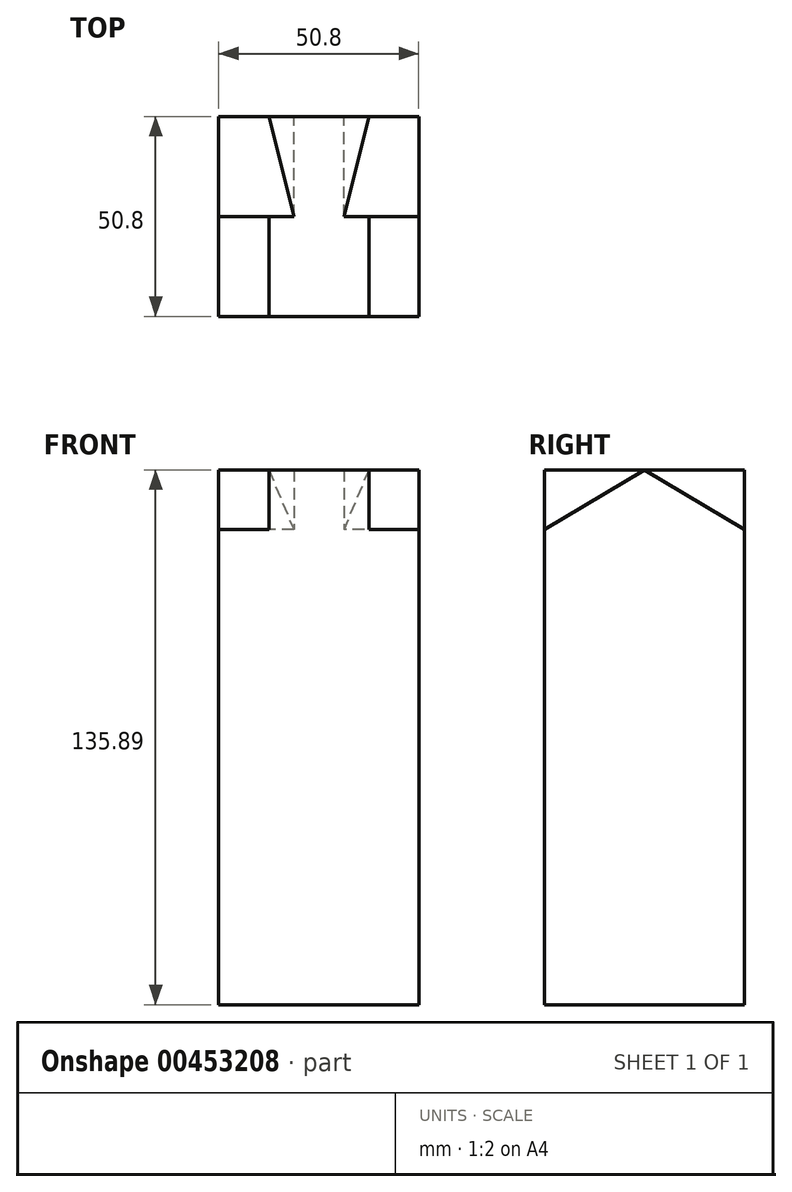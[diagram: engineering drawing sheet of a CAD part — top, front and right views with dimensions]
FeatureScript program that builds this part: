
annotation { "Feature Type Name" : "Feature", "Feature Type Description" : "" }
export const myFeature = defineFeature(function(context is Context, id is Id, definition is map)
    precondition{}
    {
        {
            var Q0;
            Q0=qCreatedBy(makeId("Top.planeOp"),FACE);
            var sketch = newSketch(context, id + "F0", { "sketchPlane" : qUnion([Q0])});
            skLineSegment(sketch, "E0.bottom", {"start": v(30.23, -20.65) * mm, "end": v(-20.57, -20.65) * mm});
            skLineSegment(sketch, "E0.top", {"start": v(30.23, 30.15) * mm, "end": v(-20.57, 30.15) * mm});
            skLineSegment(sketch, "E0.left", {"start": v(30.23, -20.65) * mm, "end": v(30.23, 30.15) * mm});
            skLineSegment(sketch, "E0.right", {"start": v(-20.57, -20.65) * mm, "end": v(-20.57, 30.15) * mm});
            skSolve(sketch);
        }
        {
            var Q0;
            Q0=makeQuery(id+"F0.imprint","IMPRINT",FACE,{"disambiguationData":[TD([[makeQuery(id+"F0.imprint","IMPRINT",EDGE,{"derivedFrom":sQuery(id+"F0.wireOp",EDGE,"E0.bottom")}),-1.0]])]});
            extrude(context, id + "F1", {"entities" : qUnion([Q0]), "depth" : 135.89 * mm});
        }
        {
            var Q0;
            Q0=makeQuery(id+"F1.opExtrude","SWEPT_FACE",FACE,{"disambiguationData":[OSD([sQuery(id+"F0.wireOp",EDGE,"E0.top")])]});
            var sketch = newSketch(context, id + "F2", { "sketchPlane" : qUnion([Q0])});
            skLineSegment(sketch, "E1", {"start": v(-17.53, 135.9) * mm, "end": v(-11.18, 120.72) * mm});
            skLineSegment(sketch, "E2", {"start": v(7.87, 135.9) * mm, "end": v(1.52, 120.72) * mm});
            skLineSegment(sketch, "E3", {"start": v(-11.18, 120.72) * mm, "end": v(1.52, 120.72) * mm});
            skLineSegment(sketch, "E4", {"start": v(-11.18, 120.72) * mm, "end": v(-30.23, 120.72) * mm});
            skLineSegment(sketch, "E5", {"start": v(1.52, 120.72) * mm, "end": v(20.57, 120.72) * mm});
            skSolve(sketch);
        }
        {
            var Q0;
            Q0=makeQuery(id+"F1.opExtrude","SWEPT_FACE",FACE,{"disambiguationData":[OSD([sQuery(id+"F0.wireOp",EDGE,"E0.right")])]});
            var sketch = newSketch(context, id + "F3", { "sketchPlane" : qUnion([Q0])});
            skLineSegment(sketch, "E6", {"start": v(-30.15, 120.72) * mm, "end": v(-4.75, 135.9) * mm});
            skLineSegment(sketch, "E7", {"start": v(-4.75, 135.9) * mm, "end": v(20.65, 120.72) * mm});
            skSolve(sketch);
        }
        {
            var Q0;
            Q0=makeQuery(id+"F1.opExtrude","CAP_FACE",FACE,{"disambiguationData":[OSD([sQuery(id+"F0.wireOp",EDGE,"E0.bottom"),sQuery(id+"F0.wireOp",EDGE,"E0.top"),sQuery(id+"F0.wireOp",EDGE,"E0.left"),sQuery(id+"F0.wireOp",EDGE,"E0.right")])],"isStart":false});
            var sketch = newSketch(context, id + "F4", { "sketchPlane" : qUnion([Q0])});
            skLineSegment(sketch, "E8", {"start": v(-7.87, 30.15) * mm, "end": v(-7.87, -20.65) * mm});
            skLineSegment(sketch, "E9", {"start": v(17.53, 30.15) * mm, "end": v(17.53, -20.65) * mm});
            skLineSegment(sketch, "E10", {"start": v(-20.57, 4.75) * mm, "end": v(30.23, 4.75) * mm});
            skLineSegment(sketch, "E11", {"start": v(17.53, 30.15) * mm, "end": v(11.18, 4.75) * mm});
            skLineSegment(sketch, "E12", {"start": v(11.18, 4.75) * mm, "end": v(-1.52, 4.75) * mm});
            skLineSegment(sketch, "E13", {"start": v(-1.52, 4.75) * mm, "end": v(-7.87, 30.15) * mm});
            skLineSegment(sketch, "E14", {"start": v(11.18, 4.75) * mm, "end": v(30.23, 4.75) * mm});
            skLineSegment(sketch, "E15", {"start": v(-1.52, 4.75) * mm, "end": v(-20.57, 4.75) * mm});
            skSolve(sketch);
        }
        {
            var Q0;
            {var subQ4=sQuery(id+"F3.wireOp",EDGE,"E6");Q0=makeQuery(id+"F3.imprint","IMPRINT",FACE,{"disambiguationData":[TD([[makeQuery(id+"F3.imprint","IMPRINT",EDGE,{"derivedFrom":subQ4}),-1.0]])]});}
            var sketch = newSketch(context, id + "F5", { "sketchPlane" : qUnion([Q0])});
            skLineSegment(sketch, "E16", {"start": v(-4.75, 135.9) * mm, "end": v(-4.75, 120.72) * mm});
            skLineSegment(sketch, "E17", {"start": v(-4.75, 120.72) * mm, "end": v(-30.15, 120.72) * mm});
            skLineSegment(sketch, "E18", {"start": v(-4.75, 135.9) * mm, "end": v(-30.15, 120.72) * mm});
            skSolve(sketch);
        }
        {
            var Q0;
            Q0 = qSketchRegion(id + "F5", true);
            var Q1;
            {var subQ0=sQuery(id+"F3.wireOp",EDGE,"E6");Q1=makeQuery(id+"F3.imprint","IMPRINT",FACE,{"disambiguationData":[TD([[makeQuery(id+"F3.imprint","IMPRINT",EDGE,{"derivedFrom":subQ0}),1.0]])]});}
            extrude(context, id + "F6", {"entities" : qUnion([Q0, Q1]), "operationType" : NewBodyOperationType.REMOVE, "oppositeDirection" : true, "depth" : 50.8 * mm});
        }
        {
            var Q0;
            Q0=makeQuery(id+"F6.boolean.opBoolean","COPY",FACE,{"derivedFrom":makeQuery(id+"F6.opExtrude","SWEPT_FACE",FACE,{"disambiguationData":[OSD([sQuery(id+"F5.wireOp",EDGE,"E16")])]})});
            var sketch = newSketch(context, id + "F7", { "sketchPlane" : qUnion([Q0])});
            skLineSegment(sketch, "E19", {"start": v(-11.18, 135.9) * mm, "end": v(-11.18, 120.72) * mm});
            skSolve(sketch);
        }
        {
            var Q0;
            Q0=makeQuery(id+"F6.boolean.opBoolean","COPY",FACE,{"derivedFrom":makeQuery(id+"F6.opExtrude","SWEPT_FACE",FACE,{"disambiguationData":[OSD([sQuery(id+"F5.wireOp",EDGE,"E17")])]})});
            var sketch = newSketch(context, id + "F8", { "sketchPlane" : qUnion([Q0])});
            skLineSegment(sketch, "E20", {"start": v(11.18, 30.15) * mm, "end": v(11.18, 4.75) * mm});
            skSolve(sketch);
        }
        {
            var Q0;
            {var subQ0=sQuery(id+"F7.wireOp",EDGE,"E19");Q0=makeQuery(id+"F7.imprint","IMPRINT",FACE,{"disambiguationData":[TD([[makeQuery(id+"F7.imprint","IMPRINT",EDGE,{"derivedFrom":subQ0}),1.0]])]});}
            var sketch = newSketch(context, id + "F9", { "sketchPlane" : qUnion([Q0])});
            skLineSegment(sketch, "E21", {"start": v(1.52, 135.9) * mm, "end": v(1.52, 120.72) * mm});
            skSolve(sketch);
        }
        {
            var Q0;
            {var subQ0=sQuery(id+"F8.wireOp",EDGE,"E20");Q0=makeQuery(id+"F8.imprint","IMPRINT",FACE,{"disambiguationData":[TD([[makeQuery(id+"F8.imprint","IMPRINT",EDGE,{"derivedFrom":subQ0}),-1.0]])]});}
            var sketch = newSketch(context, id + "F10", { "sketchPlane" : qUnion([Q0])});
            skLineSegment(sketch, "E22", {"start": v(-1.52, 4.75) * mm, "end": v(-1.52, 30.15) * mm});
            skSolve(sketch);
        }
        {
            var Q0;
            {var subQ0=sQuery(id+"F2.wireOp",EDGE,"E1");Q0=makeQuery(id+"F2.imprint","IMPRINT",FACE,{"disambiguationData":[TD([[makeQuery(id+"F2.imprint","IMPRINT",EDGE,{"derivedFrom":subQ0}),1.0]])]});}
            var sketch = newSketch(context, id + "F11", { "sketchPlane" : qUnion([Q0])});
            skLineSegment(sketch, "E23", {"start": v(-11.18, 135.9) * mm, "end": v(1.52, 135.9) * mm});
            skLineSegment(sketch, "E24", {"start": v(1.52, 135.9) * mm, "end": v(1.52, 120.72) * mm});
            skLineSegment(sketch, "E25", {"start": v(1.52, 120.72) * mm, "end": v(-11.18, 120.72) * mm});
            skLineSegment(sketch, "E26", {"start": v(-11.18, 120.72) * mm, "end": v(-11.18, 135.9) * mm});
            skSolve(sketch);
        }
        {
            var Q0;
            Q0=makeQuery(id+"F11.imprint","IMPRINT",FACE,{"disambiguationData":[TD([[makeQuery(id+"F11.imprint","IMPRINT",EDGE,{"derivedFrom":sQuery(id+"F11.wireOp",EDGE,"E23")}),-1.0]])]});
            extrude(context, id + "F12", {"entities" : qUnion([Q0]), "operationType" : NewBodyOperationType.ADD, "oppositeDirection" : true, "depth" : 27.71 * mm});
        }
        {
            var Q0;
            {var subQ0=sQuery(id+"F2.wireOp",EDGE,"E1");Q0=makeQuery(id+"F2.imprint","IMPRINT",FACE,{"disambiguationData":[TD([[makeQuery(id+"F2.imprint","IMPRINT",EDGE,{"derivedFrom":subQ0}),1.0]])]});}
            extrude(context, id + "F13", {"entities" : qUnion([Q0]), "operationType" : NewBodyOperationType.ADD, "oppositeDirection" : true, "depth" : 36.9 * mm});
        }
        {
            var Q0;
            {var subQ0=sQuery(id+"F4.wireOp",EDGE,"E11");Q0=makeQuery(id+"F4.imprint","IMPRINT",FACE,{"disambiguationData":[TD([[makeQuery(id+"F4.imprint","IMPRINT",EDGE,{"derivedFrom":subQ0}),1.0]])]});}
            extrude(context, id + "F14", {"entities" : qUnion([Q0]), "operationType" : NewBodyOperationType.REMOVE, "endBound" : BoundingType.UP_TO_NEXT, "oppositeDirection" : true, "depth" : 14.83 * mm});
        }
        {
            var Q0;
            Q0=sQuery(id+"F7.wireOp",VERTEX,"E19.start");
            var Q1;
            Q1=sQuery(id+"F8.wireOp",VERTEX,"E20.start");
            var Q2;
            {var subQ0=sQuery(id+"F2.wireOp",EDGE,"E1");Q2=makeQuery(id+"F14.boolean.opBoolean","MERGE",VERTEX,{"derivedFrom":[makeQuery(id+"F13.opExtrude","CAP_VERTEX",VERTEX,{"disambiguationData":[OSD([sQuery(id+"F0.wireOp",EDGE,"E0.top"),subQ0])],"isStart":true}),makeQuery(id+"F14.opExtrude","CAP_VERTEX",VERTEX,{"disambiguationData":[OSD([subQ0,sQuery(id+"F4.wireOp",EDGE,"E9"),sQuery(id+"F4.wireOp",EDGE,"E11"),sQuery(id+"F4.wireOp",EDGE,"E14")])],"isStart":false})]});}
            cPlane(context, id + "F15", {"entities" : qUnion([Q0, Q1, Q2]), "cplaneType" : CPlaneType.THREE_POINT, "offset" : 25.4 * mm, "width" : 152.4 * mm, "height" : 152.4 * mm});
        }
        {
            var Q0;
            Q0=qCreatedBy(id+"F15.planeOp",FACE);
            var sketch = newSketch(context, id + "F16", { "sketchPlane" : qUnion([Q0])});
            skLineSegment(sketch, "E27", {"start": v(-21.22, 132.12) * mm, "end": v(4.84, 129.67) * mm});
            skLineSegment(sketch, "E28", {"start": v(3.53, 115.68) * mm, "end": v(-21.22, 115.68) * mm});
            skLineSegment(sketch, "E29", {"start": v(-21.22, 115.68) * mm, "end": v(-21.22, 132.12) * mm});
            skLineSegment(sketch, "E30", {"start": v(4.84, 129.67) * mm, "end": v(3.53, 115.68) * mm});
            skSolve(sketch);
        }
        {
            var Q0;
            Q0 = qSketchRegion(id + "F16", true);
            extrude(context, id + "F17", {"entities" : qUnion([Q0]), "operationType" : NewBodyOperationType.REMOVE, "oppositeDirection" : true, "depth" : 5.82 * mm});
        }
        {
            var Q0;
            Q0=makeQuery(id+"F1.opExtrude","SWEPT_FACE",FACE,{"disambiguationData":[OSD([sQuery(id+"F0.wireOp",EDGE,"E0.left")])]});
            extrude(context, id + "F18", {"entities" : qUnion([Q0]), "operationType" : NewBodyOperationType.ADD, "oppositeDirection" : true, "depth" : 25.65 * mm});
        }
        {
            var Q0;
            Q0=makeQuery(id+"F1.opExtrude","SWEPT_FACE",FACE,{"disambiguationData":[OSD([sQuery(id+"F0.wireOp",EDGE,"E0.left")])]});
            var sketch = newSketch(context, id + "F19", { "sketchPlane" : qUnion([Q0])});
            skLineSegment(sketch, "E31", {"start": v(4.75, 135.9) * mm, "end": v(4.75, 120.72) * mm});
            skLineSegment(sketch, "E32", {"start": v(4.75, 120.72) * mm, "end": v(30.15, 120.72) * mm});
            skLineSegment(sketch, "E33", {"start": v(30.15, 120.72) * mm, "end": v(4.75, 135.9) * mm});
            skSolve(sketch);
        }
        {
            var Q0;
            Q0=makeQuery(id+"F19.imprint","IMPRINT",FACE,{"disambiguationData":[TD([[makeQuery(id+"F19.imprint","IMPRINT",EDGE,{"derivedFrom":sQuery(id+"F19.wireOp",EDGE,"E31")}),1.0]])]});
            extrude(context, id + "F20", {"entities" : qUnion([Q0]), "operationType" : NewBodyOperationType.ADD, "oppositeDirection" : true, "depth" : 50.8 * mm});
        }
        {
            var Q0;
            Q0=sQuery(id+"F9.wireOp",VERTEX,"E21.start");
            var Q1;
            Q1=makeQuery(id+"F13.opExtrude","CAP_VERTEX",VERTEX,{"disambiguationData":[OSD([sQuery(id+"F0.wireOp",EDGE,"E0.top"),sQuery(id+"F2.wireOp",EDGE,"E2")])],"isStart":true});
            var Q2;
            Q2=sQuery(id+"F10.wireOp",VERTEX,"E22.end");
            cPlane(context, id + "F21", {"entities" : qUnion([Q0, Q1, Q2]), "cplaneType" : CPlaneType.THREE_POINT, "offset" : 25.4 * mm, "width" : 152.4 * mm, "height" : 152.4 * mm});
        }
        {
            var Q0;
            Q0=qCreatedBy(id+"F21.planeOp",FACE);
            var sketch = newSketch(context, id + "F22", { "sketchPlane" : qUnion([Q0])});
            skLineSegment(sketch, "E34", {"start": v(19.22, 128.42) * mm, "end": v(19.22, 111.94) * mm});
            skLineSegment(sketch, "E35", {"start": v(-6.85, 125.94) * mm, "end": v(19.22, 128.42) * mm});
            skLineSegment(sketch, "E36", {"start": v(-6.85, 125.94) * mm, "end": v(-5.53, 111.94) * mm});
            skLineSegment(sketch, "E37", {"start": v(-5.53, 111.94) * mm, "end": v(19.22, 111.94) * mm});
            skSolve(sketch);
        }
        {
            var Q0;
            Q0=makeQuery(id+"F22.imprint","IMPRINT",FACE,{"disambiguationData":[TD([[makeQuery(id+"F22.imprint","IMPRINT",EDGE,{"derivedFrom":sQuery(id+"F22.wireOp",EDGE,"E34")}),-1.0]])]});
            extrude(context, id + "F23", {"entities" : qUnion([Q0]), "operationType" : NewBodyOperationType.REMOVE, "oppositeDirection" : true, "depth" : 9.9 * mm});
        }
        {
            var Q0;
            Q0=makeQuery(id+"F1.opExtrude","SWEPT_FACE",FACE,{"disambiguationData":[OSD([sQuery(id+"F0.wireOp",EDGE,"E0.right")])]});
            extrude(context, id + "F24", {"entities" : qUnion([Q0]), "operationType" : NewBodyOperationType.ADD, "oppositeDirection" : true, "depth" : 28.2 * mm});
        }
        {
            var Q0;
            {var subQ0=sQuery(id+"F0.wireOp",EDGE,"E0.top");Q0=makeQuery(id+"F13.boolean.opBoolean","MERGE",FACE,{"derivedFrom":[makeQuery(id+"F12.boolean.opBoolean","MERGE",FACE,{"derivedFrom":[makeQuery(id+"F1.opExtrude","CAP_FACE",FACE,{"disambiguationData":[OSD([sQuery(id+"F0.wireOp",EDGE,"E0.bottom"),subQ0,sQuery(id+"F0.wireOp",EDGE,"E0.left"),sQuery(id+"F0.wireOp",EDGE,"E0.right")])],"isStart":false}),makeQuery(id+"F12.opExtrude","SWEPT_FACE",FACE,{"disambiguationData":[OSD([sQuery(id+"F11.wireOp",EDGE,"E23")])]})]}),makeQuery(id+"F13.opExtrude","SWEPT_FACE",FACE,{"disambiguationData":[OSD([subQ0])]})]});}
            var sketch = newSketch(context, id + "F25", { "sketchPlane" : qUnion([Q0])});
            skLineSegment(sketch, "E38", {"start": v(-1.52, 4.75) * mm, "end": v(-7.87, 4.75) * mm});
            skLineSegment(sketch, "E39", {"start": v(-7.87, 4.75) * mm, "end": v(-7.87, 29.86) * mm});
            skSolve(sketch);
        }
        {
            var Q0;
            Q0=makeQuery(id+"F25.imprint","IMPRINT",FACE,{"disambiguationData":[TD([[makeQuery(id+"F25.imprint","IMPRINT",EDGE,{"derivedFrom":sQuery(id+"F25.wireOp",EDGE,"E38")}),-1.0]])]});
            extrude(context, id + "F26", {"entities" : qUnion([Q0]), "operationType" : NewBodyOperationType.REMOVE, "oppositeDirection" : true, "depth" : 3.56 * mm});
        }
        {
            var Q0;
            Q0=makeQuery(id+"F20.boolean.opBoolean","MERGE",FACE,{"derivedFrom":[makeQuery(id+"F1.opExtrude","SWEPT_FACE",FACE,{"disambiguationData":[OSD([sQuery(id+"F0.wireOp",EDGE,"E0.right")])]}),makeQuery(id+"F20.opExtrude","CAP_FACE",FACE,{"disambiguationData":[OSD([sQuery(id+"F19.wireOp",EDGE,"E31"),sQuery(id+"F19.wireOp",EDGE,"E32"),sQuery(id+"F19.wireOp",EDGE,"E33")])],"isStart":false})]});
            extrude(context, id + "F27", {"entities" : qUnion([Q0]), "operationType" : NewBodyOperationType.ADD, "oppositeDirection" : true, "depth" : 33.53 * mm});
        }
        {
            var Q0;
            Q0=makeQuery(id+"F20.boolean.opBoolean","MERGE",FACE,{"derivedFrom":[makeQuery(id+"F1.opExtrude","SWEPT_FACE",FACE,{"disambiguationData":[OSD([sQuery(id+"F0.wireOp",EDGE,"E0.left")])]}),makeQuery(id+"F20.opExtrude","CAP_FACE",FACE,{"disambiguationData":[OSD([sQuery(id+"F19.wireOp",EDGE,"E31"),sQuery(id+"F19.wireOp",EDGE,"E32"),sQuery(id+"F19.wireOp",EDGE,"E33")])],"isStart":true})]});
            var sketch = newSketch(context, id + "F28", { "sketchPlane" : qUnion([Q0])});
            skLineSegment(sketch, "E40", {"start": v(30.15, 120.72) * mm, "end": v(-20.65, 120.72) * mm});
            skLineSegment(sketch, "E41", {"start": v(-20.65, 120.72) * mm, "end": v(4.75, 135.9) * mm});
            skLineSegment(sketch, "E42", {"start": v(4.75, 135.9) * mm, "end": v(30.15, 120.72) * mm});
            skSolve(sketch);
        }
        {
            var Q0;
            {var subQ0=sQuery(id+"F28.wireOp",EDGE,"E41");Q0=makeQuery(id+"F28.imprint","IMPRINT",FACE,{"disambiguationData":[TD([[makeQuery(id+"F28.imprint","IMPRINT",EDGE,{"derivedFrom":subQ0}),1.0]])]});}
            extrude(context, id + "F29", {"entities" : qUnion([Q0]), "operationType" : NewBodyOperationType.REMOVE, "oppositeDirection" : true, "depth" : 12.7 * mm});
        }
        {
            var Q0;
            Q0=makeQuery(id+"F20.boolean.opBoolean","MERGE",FACE,{"derivedFrom":[makeQuery(id+"F1.opExtrude","SWEPT_FACE",FACE,{"disambiguationData":[OSD([sQuery(id+"F0.wireOp",EDGE,"E0.right")])]}),makeQuery(id+"F20.opExtrude","CAP_FACE",FACE,{"disambiguationData":[OSD([sQuery(id+"F19.wireOp",EDGE,"E31"),sQuery(id+"F19.wireOp",EDGE,"E32"),sQuery(id+"F19.wireOp",EDGE,"E33")])],"isStart":false})]});
            var sketch = newSketch(context, id + "F30", { "sketchPlane" : qUnion([Q0])});
            skLineSegment(sketch, "E43", {"start": v(-30.15, 120.72) * mm, "end": v(20.65, 120.72) * mm});
            skLineSegment(sketch, "E44", {"start": v(-4.75, 135.9) * mm, "end": v(20.65, 120.72) * mm});
            skSolve(sketch);
        }
        {
            var Q0;
            {var subQ0=sQuery(id+"F30.wireOp",EDGE,"E44");Q0=makeQuery(id+"F30.imprint","IMPRINT",FACE,{"disambiguationData":[TD([[makeQuery(id+"F30.imprint","IMPRINT",EDGE,{"derivedFrom":subQ0}),1.0]])]});}
            extrude(context, id + "F31", {"entities" : qUnion([Q0]), "operationType" : NewBodyOperationType.REMOVE, "oppositeDirection" : true, "depth" : 12.7 * mm});
        }
    });
